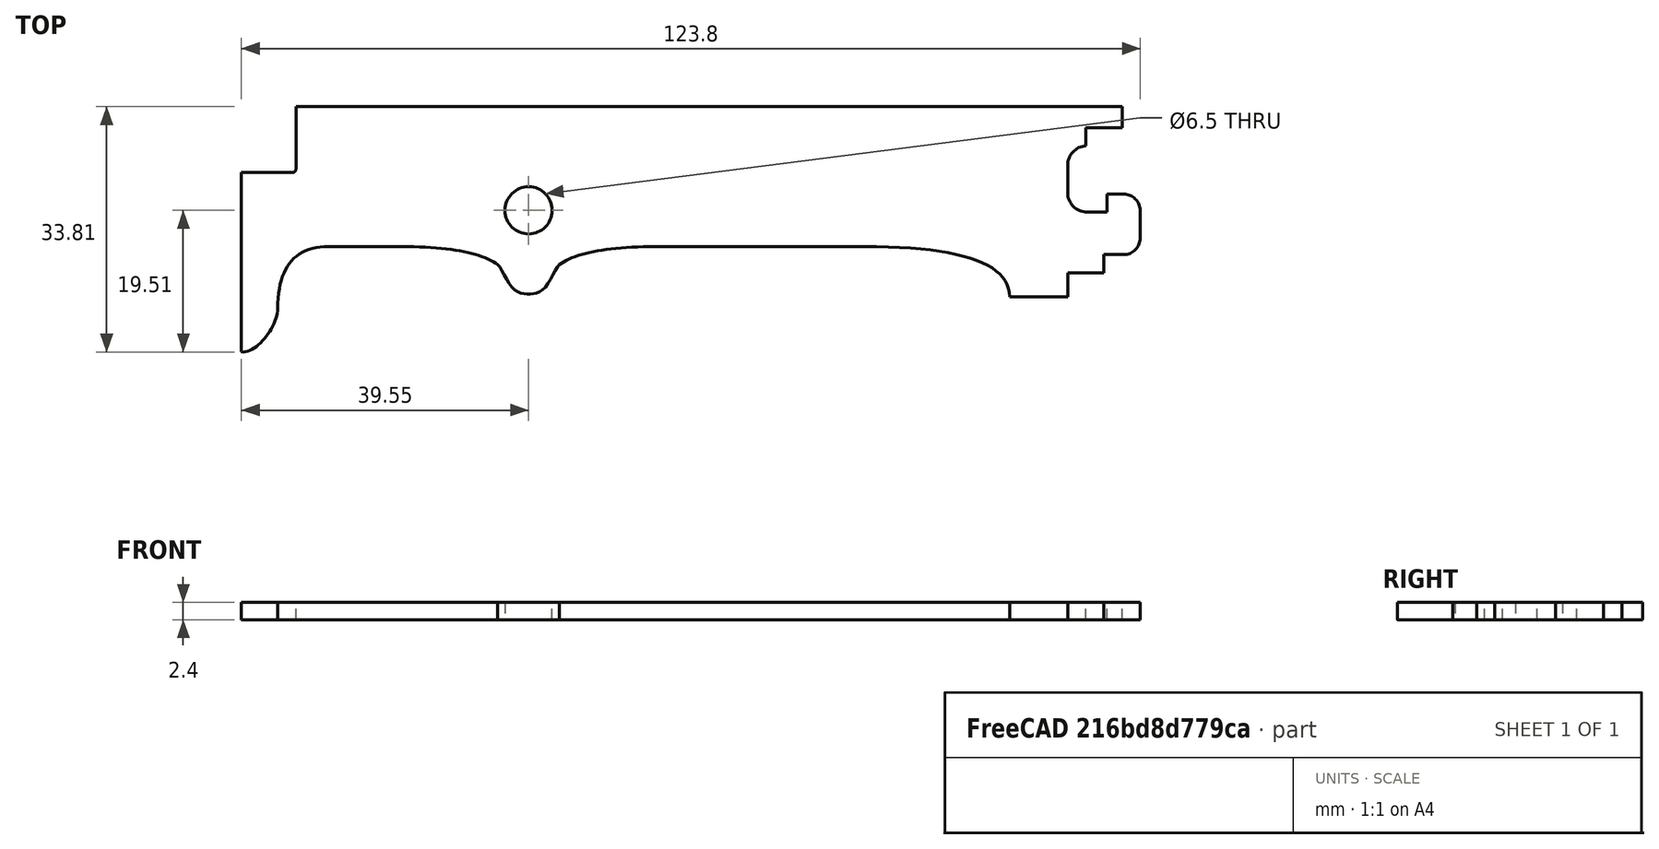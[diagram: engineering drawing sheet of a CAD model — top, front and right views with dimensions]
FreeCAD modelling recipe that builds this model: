
FCSTD DOCUMENT  (FreeCAD 0.19R0.19.2)
Label: v0_14
License: All rights reserved
LicenseURL: http://en.wikipedia.org/wiki/All_rights_reserved
objects: Sketcher::SketchObject×2, Part::Extrusion×1
note: 3 computed .brp shape members not serialized (recipe doc carries the construction recipe); baked Part::Feature solids carry a one-line shape summary decoded from their .brp

FEATURE [Sketcher::SketchObject] Sketch
  FullyConstrained = true
  sketch-geometry (69):
    g0: ArcOfCircle CenterX=-20 CenterY=-14.35 CenterZ=0 NormalX=0 NormalY=0 NormalZ=1 AngleXU=0 Radius=2.3 StartAngle=8e-16 EndAngle=1.5708
    g1: ArcOfCircle CenterX=-20 CenterY=-18.1 CenterZ=0 NormalX=0 NormalY=0 NormalZ=1 AngleXU=0 Radius=2.3 StartAngle=4.71239 EndAngle=6.28319
    g2: LineSegment StartX=-20 StartY=-20.4 StartZ=0 EndX=-22.7 EndY=-20.4 EndZ=0
    g3: LineSegment StartX=-22.7 StartY=-22.9 StartZ=0 EndX=-22.7 EndY=-20.4 EndZ=0
    g4: LineSegment StartX=-17.7 StartY=-14.35 StartZ=0 EndX=-17.7 EndY=-18.1 EndZ=0
    g5: LineSegment StartX=-25.2 StartY=-5.40742 StartZ=0 EndX=-25.2 EndY=-2.9 EndZ=0
    g6: LineSegment StartX=-25.2 StartY=-2.9 StartZ=0 EndX=-20.2 EndY=-2.9 EndZ=0
    g7: LineSegment StartX=-20.2 StartY=-2.9 StartZ=0 EndX=-20.2 EndY=0 EndZ=0
    g8: ArcOfCircle CenterX=-25 CenterY=-8.1 CenterZ=0 NormalX=0 NormalY=0 NormalZ=1 AngleXU=0 Radius=2.7 StartAngle=1.64494 EndAngle=3.14159
    g9: ArcOfCircle CenterX=-25 CenterY=-11.85 CenterZ=0 NormalX=0 NormalY=0 NormalZ=1 AngleXU=0 Radius=2.7 StartAngle=3.14159 EndAngle=4.71239
    g10: LineSegment StartX=-27.7 StartY=-8.1 StartZ=0 EndX=-27.7 EndY=-11.85 EndZ=0
    g11: LineSegment StartX=-25 StartY=-14.55 StartZ=0 EndX=-22.3 EndY=-14.55 EndZ=0
    g12: LineSegment StartX=-22.3 StartY=-12.05 StartZ=0 EndX=-22.3 EndY=-14.55 EndZ=0
    g13: LineSegment StartX=-22.3 StartY=-12.05 StartZ=0 EndX=-20 EndY=-12.05 EndZ=0
    g14: LineSegment StartX=-27.7 StartY=-22.9 StartZ=0 EndX=-22.7 EndY=-22.9 EndZ=0
    g15: LineSegment StartX=-27.7 StartY=-22.9 StartZ=0 EndX=-27.7 EndY=-26.2 EndZ=0
    g16: Circle CenterX=-101.95 CenterY=-14.3 CenterZ=0 NormalX=0 NormalY=0 NormalZ=1 AngleXU=0 Radius=3.25
    g17: LineSegment StartX=-134 StartY=0 StartZ=0 EndX=-20.2 EndY=0 EndZ=0
    g18: LineSegment StartX=-134 StartY=2.68e-14 StartZ=0 EndX=-134 EndY=-8.6 EndZ=0
    g19: LineSegment StartX=-134.5 StartY=-9.1 StartZ=0 EndX=-141.5 EndY=-9.1 EndZ=0
    g20: ArcOfCircle CenterX=-134.5 CenterY=-8.6 CenterZ=0 NormalX=0 NormalY=0 NormalZ=1 AngleXU=0 Radius=0.5 StartAngle=4.71239 EndAngle=6.28319
    g21: Circle CenterX=-97.7 CenterY=-21.8 CenterZ=0 NormalX=0 NormalY=0 NormalZ=1 AngleXU=0 Radius=1
    g22: Circle CenterX=-94.45 CenterY=-19.3 CenterZ=0 NormalX=0 NormalY=0 NormalZ=1 AngleXU=0 Radius=1
    g23: Circle CenterX=-84.45 CenterY=-19.3 CenterZ=0 NormalX=0 NormalY=0 NormalZ=1 AngleXU=0 Radius=1
    g24: BSplineCurve PolesCount=3 KnotsCount=2 Degree=2 IsPeriodic=0
    g25: GeomPoint X=-97.7 Y=-21.8 Z=0
    g26: GeomPoint X=-84.45 Y=-19.3 Z=0
    g27: Circle CenterX=-106.2 CenterY=-21.8 CenterZ=0 NormalX=0 NormalY=0 NormalZ=1 AngleXU=0 Radius=1
    g28: Circle CenterX=-109.45 CenterY=-19.3 CenterZ=0 NormalX=0 NormalY=0 NormalZ=1 AngleXU=0 Radius=1
    g29: Circle CenterX=-119.45 CenterY=-19.3 CenterZ=0 NormalX=0 NormalY=0 NormalZ=1 AngleXU=0 Radius=1
    g30: BSplineCurve PolesCount=3 KnotsCount=2 Degree=2 IsPeriodic=0
    g31: GeomPoint X=-106.2 Y=-21.8 Z=0
    g32: GeomPoint X=-119.45 Y=-19.3 Z=0
    g33: LineSegment StartX=-141.5 StartY=-9.1 StartZ=0 EndX=-141.5 EndY=-33.8 EndZ=0
    g34-g37: Circle x4 (B-spline internal-alignment scaffolding for g38; pole/knot coordinates omitted)
    g38: BSplineCurve PolesCount=4 KnotsCount=2 Degree=3 IsPeriodic=0
    g39: GeomPoint X=-141.5 Y=-33.8 Z=0
    g40: GeomPoint X=-136.5 Y=-27.8 Z=0
    g41: Circle CenterX=-136.5 CenterY=-27.8 CenterZ=0 NormalX=0 NormalY=0 NormalZ=1 AngleXU=0 Radius=1
    g42: Circle CenterX=-136.5 CenterY=-19.3 CenterZ=0 NormalX=0 NormalY=0 NormalZ=1 AngleXU=0 Radius=1
    g43: Circle CenterX=-129.5 CenterY=-19.3 CenterZ=0 NormalX=0 NormalY=0 NormalZ=1 AngleXU=0 Radius=1
    g44: BSplineCurve PolesCount=3 KnotsCount=2 Degree=2 IsPeriodic=0
    g45: GeomPoint X=-136.5 Y=-27.8 Z=0
    g46: GeomPoint X=-129.5 Y=-19.3 Z=0
    g47: LineSegment StartX=-129.5 StartY=-19.3 StartZ=0 EndX=-119.45 EndY=-19.3 EndZ=0
    g48: LineSegment StartX=-35.7 StartY=-26.2 StartZ=0 EndX=-27.7 EndY=-26.2 EndZ=0
    g49: Circle CenterX=-35.7 CenterY=-26.2 CenterZ=0 NormalX=0 NormalY=0 NormalZ=1 AngleXU=0 Radius=1
    g50: Circle CenterX=-35.7 CenterY=-19.3 CenterZ=0 NormalX=0 NormalY=0 NormalZ=1 AngleXU=0 Radius=1
    g51: Circle CenterX=-55.7 CenterY=-19.3 CenterZ=0 NormalX=0 NormalY=0 NormalZ=1 AngleXU=0 Radius=1
    g52: BSplineCurve PolesCount=3 KnotsCount=2 Degree=2 IsPeriodic=0
    g53: GeomPoint X=-35.7 Y=-26.2 Z=0
    g54: GeomPoint X=-55.7 Y=-19.3 Z=0
    g55: LineSegment StartX=-84.45 StartY=-19.3 StartZ=0 EndX=-55.7 EndY=-19.3 EndZ=0
    g56-g62: Circle x7 (B-spline internal-alignment scaffolding for g63; pole/knot coordinates omitted)
    g63: BSplineCurve PolesCount=7 KnotsCount=5 Degree=3 IsPeriodic=0
    g64-g68: GeomPoint x5 (B-spline internal-alignment scaffolding for g63; pole/knot coordinates omitted)
  constraints (111):
    c: Block(g1)
    c: Block(g0)
    c: Coincident(g2,g1)
    c: Horizontal(g2)
    c: Vertical(g3)
    c: Coincident(g3,g2)
    c: Coincident(g4,g0)
    c: Coincident(g4,g1)
    c: Vertical(g4)
    c: Vertical(g5)
    c: Block(g5)
    c: Coincident(g6,g5)
    c: Horizontal(g6)
    c: Vertical(g7)
    c: Block(g7)
    c: Block(g6)
    c: Coincident(g8,g5)
    c: Block(g9)
    c: Coincident(g10,g8)
    c: Coincident(g10,g9)
    c: Vertical(g10)
    c: Block(g10)
    c: Coincident(g11,g9)
    c: Horizontal(g11)
    c: Vertical(g12)
    c: Coincident(g12,g11)
    c: Block(g12)
    c: Coincident(g13,g0)
    c: Horizontal(g13)
    c: Block(g13)
    c: Coincident(g14,g3)
    c: Horizontal(g14)
    c: Block(g14)
    c: Coincident(g15,g14)
    c: Vertical(g15)
    c: Block(g16)
    c: Coincident(g17,g7)
    c: Horizontal(g17)
    c: Vertical(g18)
    c: Distance(g18) = 8.6
    c: Horizontal(g19)
    c: Distance(g19) = 7
    c: Coincident(g20,g18)
    c: Coincident(g20,g19)
    c: Block(g20)
    c: Block(g17)
    c: Weight(g21) = 1
    c: Equal(g21,g22)
    c: Equal(g21,g23)
    c: InternalAlignment(g21,g24)
    c: InternalAlignment(g22,g24)
    c: InternalAlignment(g23,g24)
    c: InternalAlignment(g25,g24)
    c: InternalAlignment(g26,g24)
    c: Weight(g27) = 1
    c: Equal(g27,g28)
    c: Equal(g27,g29)
    c: InternalAlignment(g27,g30)
    c: InternalAlignment(g28,g30)
    c: InternalAlignment(g29,g30)
    c: InternalAlignment(g31,g30)
    c: InternalAlignment(g32,g30)
    c: Block(g30)
    c: Block(g24)
    c: Coincident(g33,g19)
    c: Vertical(g33)
    c: Block(g33)
    c: Coincident(g38,g33)
    c: Weight(g34) = 1
    c: Equal(g34,g35)
    c: Equal(g34,g36)
    c: Equal(g34,g37)
    c: InternalAlignment(g34-g37 -> g38) x4
    c: InternalAlignment(g39,g38)
    c: InternalAlignment(g40,g38)
    c: Weight(g41) = 1
    c: Equal(g41,g42)
    c: Equal(g41,g43)
    c: InternalAlignment(g41,g44)
    c: InternalAlignment(g42,g44)
    c: InternalAlignment(g43,g44)
    c: InternalAlignment(g45,g44)
    c: InternalAlignment(g46,g44)
    c: Block(g38)
    c: Block(g44)
    c: Coincident(g47,g44)
    c: Coincident(g47,g30)
    c: Horizontal(g47)
    c: Horizontal(g48)
    c: Distance(g48) = 8
    c: Block(g48)
    c: Block(g15)
    c: Block(g8)
    c: Coincident(g52,g48)
    c: Weight(g49) = 1
    c: Equal(g49,g50)
    c: Equal(g49,g51)
    c: InternalAlignment(g49,g52)
    c: InternalAlignment(g50,g52)
    c: InternalAlignment(g51,g52)
    c: InternalAlignment(g53,g52)
    c: InternalAlignment(g54,g52)
    c: Block(g52)
    c: Coincident(g55,g24)
    c: Coincident(g55,g52)
    c: Horizontal(g55)
    c: Weight(g56) = 1
    c: Equal(g56, g57-g62) x6
    c: InternalAlignment(g56-g62 -> g63) x7
    c: InternalAlignment(g64-g68 -> g63) x5
    c: Block(g63)
FEATURE [Part::Extrusion] Extrude
  Base = -> Sketch
  Dir = (0,0,1)
  DirMode = 2
  FaceMakerClass = Part::FaceMakerBullseye
  LengthFwd = 2.4
  LengthRev = 0
  Solid = true
  Symmetric = false
FEATURE [Sketcher::SketchObject] Sketch001
  FullyConstrained = true
  sketch-geometry (99):
    g0: ArcOfCircle CenterX=-20 CenterY=-14.35 CenterZ=0 NormalX=0 NormalY=0 NormalZ=1 AngleXU=0 Radius=2.3 StartAngle=8e-16 EndAngle=1.5708
    g1: ArcOfCircle CenterX=-20 CenterY=-18.1 CenterZ=0 NormalX=0 NormalY=0 NormalZ=1 AngleXU=0 Radius=2.3 StartAngle=4.71239 EndAngle=6.28319
    g2: LineSegment StartX=-20 StartY=-20.4 StartZ=0 EndX=-22.7 EndY=-20.4 EndZ=0
    g3: LineSegment StartX=-22.7 StartY=-22.9 StartZ=0 EndX=-22.7 EndY=-20.4 EndZ=0
    g4: LineSegment StartX=-17.7 StartY=-14.35 StartZ=0 EndX=-17.7 EndY=-18.1 EndZ=0
    g5: LineSegment StartX=-25.2 StartY=-5.40742 StartZ=0 EndX=-25.2 EndY=-2.9 EndZ=0
    g6: LineSegment StartX=-25.2 StartY=-2.9 StartZ=0 EndX=-20.2 EndY=-2.9 EndZ=0
    g7: LineSegment StartX=-20.2 StartY=-2.9 StartZ=0 EndX=-20.2 EndY=0 EndZ=0
    g8: ArcOfCircle CenterX=-25 CenterY=-8.1 CenterZ=0 NormalX=0 NormalY=0 NormalZ=1 AngleXU=0 Radius=2.7 StartAngle=1.64494 EndAngle=3.14159
    g9: ArcOfCircle CenterX=-25 CenterY=-11.85 CenterZ=0 NormalX=0 NormalY=0 NormalZ=1 AngleXU=0 Radius=2.7 StartAngle=3.14159 EndAngle=4.71239
    g10: LineSegment StartX=-27.7 StartY=-8.1 StartZ=0 EndX=-27.7 EndY=-11.85 EndZ=0
    g11: LineSegment StartX=-25 StartY=-14.55 StartZ=0 EndX=-22.3 EndY=-14.55 EndZ=0
    g12: LineSegment StartX=-22.3 StartY=-12.05 StartZ=0 EndX=-22.3 EndY=-14.55 EndZ=0
    g13: LineSegment StartX=-22.3 StartY=-12.05 StartZ=0 EndX=-20 EndY=-12.05 EndZ=0
    g14: LineSegment StartX=-27.7 StartY=-22.9 StartZ=0 EndX=-22.7 EndY=-22.9 EndZ=0
    g15: LineSegment StartX=-27.7 StartY=-22.9 StartZ=0 EndX=-27.7 EndY=-26.2 EndZ=0
    g16: Circle CenterX=-101.95 CenterY=-14.3 CenterZ=0 NormalX=0 NormalY=0 NormalZ=1 AngleXU=0 Radius=3.25
    g17: LineSegment StartX=-134 StartY=0 StartZ=0 EndX=-134 EndY=-8.6 EndZ=0
    g18: LineSegment StartX=-134.5 StartY=-9.1 StartZ=0 EndX=-141.5 EndY=-9.1 EndZ=0
    g19: ArcOfCircle CenterX=-134.5 CenterY=-8.6 CenterZ=0 NormalX=0 NormalY=0 NormalZ=1 AngleXU=0 Radius=0.5 StartAngle=4.71239 EndAngle=6.28319
    g20: Circle CenterX=-97.7 CenterY=-21.8 CenterZ=0 NormalX=0 NormalY=0 NormalZ=1 AngleXU=0 Radius=1
    g21: Circle CenterX=-94.45 CenterY=-19.3 CenterZ=0 NormalX=0 NormalY=0 NormalZ=1 AngleXU=0 Radius=1
    g22: Circle CenterX=-84.45 CenterY=-19.3 CenterZ=0 NormalX=0 NormalY=0 NormalZ=1 AngleXU=0 Radius=1
    g23: BSplineCurve PolesCount=3 KnotsCount=2 Degree=2 IsPeriodic=0
    g24: GeomPoint X=-97.7 Y=-21.8 Z=0
    g25: GeomPoint X=-84.45 Y=-19.3 Z=0
    g26: Circle CenterX=-106.2 CenterY=-21.8 CenterZ=0 NormalX=0 NormalY=0 NormalZ=1 AngleXU=0 Radius=1
    g27: Circle CenterX=-109.45 CenterY=-19.3 CenterZ=0 NormalX=0 NormalY=0 NormalZ=1 AngleXU=0 Radius=1
    g28: Circle CenterX=-119.45 CenterY=-19.3 CenterZ=0 NormalX=0 NormalY=0 NormalZ=1 AngleXU=0 Radius=1
    g29: BSplineCurve PolesCount=3 KnotsCount=2 Degree=2 IsPeriodic=0
    g30: GeomPoint X=-106.2 Y=-21.8 Z=0
    g31: GeomPoint X=-119.45 Y=-19.3 Z=0
    g32: LineSegment StartX=-141.5 StartY=-9.1 StartZ=0 EndX=-141.5 EndY=-33.8 EndZ=0
    g33-g36: Circle x4 (B-spline internal-alignment scaffolding for g37; pole/knot coordinates omitted)
    g37: BSplineCurve PolesCount=4 KnotsCount=2 Degree=3 IsPeriodic=0
    g38: GeomPoint X=-141.5 Y=-33.8 Z=0
    g39: GeomPoint X=-136.5 Y=-27.8 Z=0
    g40: Circle CenterX=-136.5 CenterY=-27.8 CenterZ=0 NormalX=0 NormalY=0 NormalZ=1 AngleXU=0 Radius=1
    g41: Circle CenterX=-136.5 CenterY=-19.3 CenterZ=0 NormalX=0 NormalY=0 NormalZ=1 AngleXU=0 Radius=1
    g42: Circle CenterX=-129.5 CenterY=-19.3 CenterZ=0 NormalX=0 NormalY=0 NormalZ=1 AngleXU=0 Radius=1
    g43: BSplineCurve PolesCount=3 KnotsCount=2 Degree=2 IsPeriodic=0
    g44: GeomPoint X=-136.5 Y=-27.8 Z=0
    g45: GeomPoint X=-129.5 Y=-19.3 Z=0
    g46: LineSegment StartX=-129.5 StartY=-19.3 StartZ=0 EndX=-119.45 EndY=-19.3 EndZ=0
    g47: LineSegment StartX=-35.7 StartY=-26.2 StartZ=0 EndX=-27.7 EndY=-26.2 EndZ=0
    g48: Circle CenterX=-35.7 CenterY=-26.2 CenterZ=0 NormalX=0 NormalY=0 NormalZ=1 AngleXU=0 Radius=1
    g49: Circle CenterX=-35.7 CenterY=-19.3 CenterZ=0 NormalX=0 NormalY=0 NormalZ=1 AngleXU=0 Radius=1
    g50: Circle CenterX=-55.7 CenterY=-19.3 CenterZ=0 NormalX=0 NormalY=0 NormalZ=1 AngleXU=0 Radius=1
    g51: BSplineCurve PolesCount=3 KnotsCount=2 Degree=2 IsPeriodic=0
    g52: GeomPoint X=-35.7 Y=-26.2 Z=0
    g53: GeomPoint X=-55.7 Y=-19.3 Z=0
    g54: LineSegment StartX=-84.45 StartY=-19.3 StartZ=0 EndX=-55.7 EndY=-19.3 EndZ=0
    g55-g61: Circle x7 (B-spline internal-alignment scaffolding for g62; pole/knot coordinates omitted)
    g62: BSplineCurve PolesCount=7 KnotsCount=5 Degree=3 IsPeriodic=0
    g63-g67: GeomPoint x5 (B-spline internal-alignment scaffolding for g62; pole/knot coordinates omitted)
    g68: LineSegment StartX=-134 StartY=0 StartZ=0 EndX=-20.2 EndY=0 EndZ=0
    g69: ArcOfCircle CenterX=-101.95 CenterY=-14.3 CenterZ=0 NormalX=0 NormalY=0 NormalZ=1 AngleXU=0 Radius=4.69707 StartAngle=3.58144 EndAngle=5.84334
    g70: Circle CenterX=-40.7 CenterY=-3 CenterZ=0 NormalX=0 NormalY=0 NormalZ=1 AngleXU=0 Radius=1
    g71: Circle CenterX=-35.7 CenterY=-3 CenterZ=0 NormalX=0 NormalY=0 NormalZ=1 AngleXU=0 Radius=1
    g72: Circle CenterX=-35.7 CenterY=-8 CenterZ=0 NormalX=0 NormalY=0 NormalZ=1 AngleXU=0 Radius=1
    g73: BSplineCurve PolesCount=3 KnotsCount=2 Degree=2 IsPeriodic=0
    g74: GeomPoint X=-40.7 Y=-3 Z=0
    g75: GeomPoint X=-35.7 Y=-8 Z=0
    g76: Circle CenterX=-35.7 CenterY=-11.3 CenterZ=0 NormalX=0 NormalY=0 NormalZ=1 AngleXU=0 Radius=1
    g77: Circle CenterX=-35.7 CenterY=-16.3 CenterZ=0 NormalX=0 NormalY=0 NormalZ=1 AngleXU=0 Radius=1
    g78: Circle CenterX=-40.7 CenterY=-16.3 CenterZ=0 NormalX=0 NormalY=0 NormalZ=1 AngleXU=0 Radius=1
    g79: BSplineCurve PolesCount=3 KnotsCount=2 Degree=2 IsPeriodic=0
    g80: GeomPoint X=-35.7 Y=-11.3 Z=0
    g81: GeomPoint X=-40.7 Y=-16.3 Z=0
    g82: Circle CenterX=-124.5 CenterY=-16.3 CenterZ=0 NormalX=0 NormalY=0 NormalZ=1 AngleXU=0 Radius=1
    g83: Circle CenterX=-129.5 CenterY=-16.3 CenterZ=0 NormalX=0 NormalY=0 NormalZ=1 AngleXU=0 Radius=1
    g84: Circle CenterX=-129.5 CenterY=-11.3 CenterZ=0 NormalX=0 NormalY=0 NormalZ=1 AngleXU=0 Radius=1
    g85: BSplineCurve PolesCount=3 KnotsCount=2 Degree=2 IsPeriodic=0
    g86: GeomPoint X=-124.5 Y=-16.3 Z=0
    g87: GeomPoint X=-129.5 Y=-11.3 Z=0
    g88: Circle CenterX=-129.5 CenterY=-8 CenterZ=0 NormalX=0 NormalY=0 NormalZ=1 AngleXU=0 Radius=1
    g89: Circle CenterX=-129.5 CenterY=-3 CenterZ=0 NormalX=0 NormalY=0 NormalZ=1 AngleXU=0 Radius=1
    g90: Circle CenterX=-124.5 CenterY=-3 CenterZ=0 NormalX=0 NormalY=0 NormalZ=1 AngleXU=0 Radius=1
    g91: BSplineCurve PolesCount=3 KnotsCount=2 Degree=2 IsPeriodic=0
    g92: GeomPoint X=-129.5 Y=-8 Z=0
    g93: GeomPoint X=-124.5 Y=-3 Z=0
    g94: LineSegment StartX=-129.5 StartY=-8 StartZ=0 EndX=-129.5 EndY=-11.3 EndZ=0
    g95: LineSegment StartX=-124.5 StartY=-3 StartZ=0 EndX=-40.7 EndY=-3 EndZ=0
    g96: LineSegment StartX=-35.7 StartY=-8 StartZ=0 EndX=-35.7 EndY=-11.3 EndZ=0
    g97: LineSegment StartX=-40.7 StartY=-16.3 StartZ=0 EndX=-97.7 EndY=-16.3 EndZ=0
    g98: LineSegment StartX=-106.2 StartY=-16.3 StartZ=0 EndX=-124.5 EndY=-16.3 EndZ=0
  constraints (164):
    c: Block(g1)
    c: Block(g0)
    c: Coincident(g2,g1)
    c: Horizontal(g2)
    c: Vertical(g3)
    c: Coincident(g3,g2)
    c: Coincident(g4,g0)
    c: Coincident(g4,g1)
    c: Vertical(g4)
    c: Vertical(g5)
    c: Block(g5)
    c: Coincident(g6,g5)
    c: Horizontal(g6)
    c: Vertical(g7)
    c: Block(g7)
    c: Block(g6)
    c: Coincident(g8,g5)
    c: Block(g9)
    c: Coincident(g10,g8)
    c: Coincident(g10,g9)
    c: Vertical(g10)
    c: Block(g10)
    c: Coincident(g11,g9)
    c: Horizontal(g11)
    c: Vertical(g12)
    c: Coincident(g12,g11)
    c: Block(g12)
    c: Coincident(g13,g0)
    c: Horizontal(g13)
    c: Block(g13)
    c: Coincident(g14,g3)
    c: Horizontal(g14)
    c: Block(g14)
    c: Coincident(g15,g14)
    c: Vertical(g15)
    c: Block(g16)
    c: Vertical(g17)
    c: Distance(g17) = 8.6
    c: Horizontal(g18)
    c: Distance(g18) = 7
    c: Coincident(g19,g17)
    c: Coincident(g19,g18)
    c: Block(g19)
    c: Weight(g20) = 1
    c: Equal(g20,g21)
    c: Equal(g20,g22)
    c: InternalAlignment(g20,g23)
    c: InternalAlignment(g21,g23)
    c: InternalAlignment(g22,g23)
    c: InternalAlignment(g24,g23)
    c: InternalAlignment(g25,g23)
    c: Weight(g26) = 1
    c: Equal(g26,g27)
    c: Equal(g26,g28)
    c: InternalAlignment(g26,g29)
    c: InternalAlignment(g27,g29)
    c: InternalAlignment(g28,g29)
    c: InternalAlignment(g30,g29)
    c: InternalAlignment(g31,g29)
    c: Block(g23)
    c: Coincident(g32,g18)
    c: Vertical(g32)
    c: Block(g32)
    c: Coincident(g37,g32)
    c: Weight(g33) = 1
    c: Equal(g33,g34)
    c: Equal(g33,g35)
    c: Equal(g33,g36)
    c: InternalAlignment(g33-g36 -> g37) x4
    c: InternalAlignment(g38,g37)
    c: InternalAlignment(g39,g37)
    c: Weight(g40) = 1
    c: Equal(g40,g41)
    c: Equal(g40,g42)
    c: InternalAlignment(g40,g43)
    c: InternalAlignment(g41,g43)
    c: InternalAlignment(g42,g43)
    c: InternalAlignment(g44,g43)
    c: InternalAlignment(g45,g43)
    c: Block(g37)
    c: Coincident(g46,g43)
    c: Coincident(g46,g29)
    c: Horizontal(g46)
    c: Horizontal(g47)
    c: Distance(g47) = 8
    c: Block(g47)
    c: Block(g15)
    c: Block(g8)
    c: Coincident(g51,g47)
    c: Weight(g48) = 1
    c: Equal(g48,g49)
    c: Equal(g48,g50)
    c: InternalAlignment(g48,g51)
    c: InternalAlignment(g49,g51)
    c: InternalAlignment(g50,g51)
    c: InternalAlignment(g52,g51)
    c: InternalAlignment(g53,g51)
    c: Block(g51)
    c: Coincident(g54,g23)
    c: Coincident(g54,g51)
    c: Horizontal(g54)
    c: Weight(g55) = 1
    c: Equal(g55, g56-g61) x6
    c: InternalAlignment(g55-g61 -> g62) x7
    c: InternalAlignment(g63-g67 -> g62) x5
    c: Block(g62)
    c: Coincident(g68,g17)
    c: Coincident(g68,g7)
    c: Horizontal(g68)
    c: Coincident(g69,g16)
    c: Block(g69)
    c: Block(g29)
    c: Block(g43)
    c: Weight(g70) = 1
    c: Equal(g70,g71)
    c: Equal(g70,g72)
    c: InternalAlignment(g70,g73)
    c: InternalAlignment(g71,g73)
    c: InternalAlignment(g72,g73)
    c: InternalAlignment(g74,g73)
    c: InternalAlignment(g75,g73)
    c: Weight(g76) = 1
    c: Equal(g76,g77)
    c: Equal(g76,g78)
    c: InternalAlignment(g76,g79)
    c: InternalAlignment(g77,g79)
    c: InternalAlignment(g78,g79)
    c: InternalAlignment(g80,g79)
    c: InternalAlignment(g81,g79)
    c: Weight(g82) = 1
    c: Equal(g82,g83)
    c: Equal(g82,g84)
    c: InternalAlignment(g82,g85)
    c: InternalAlignment(g83,g85)
    c: InternalAlignment(g84,g85)
    c: InternalAlignment(g86,g85)
    c: InternalAlignment(g87,g85)
    c: Weight(g88) = 1
    c: Equal(g88,g89)
    c: Equal(g88,g90)
    c: InternalAlignment(g88,g91)
    c: InternalAlignment(g89,g91)
    c: InternalAlignment(g90,g91)
    c: InternalAlignment(g92,g91)
    c: InternalAlignment(g93,g91)
    c: Block(g91)
    c: Block(g85)
    c: Block(g79)
    c: Block(g73)
    c: Coincident(g94,g91)
    c: Coincident(g94,g85)
    c: Vertical(g94)
    c: Coincident(g95,g91)
    c: Horizontal(g95)
    c: Coincident(g96,g73)
    c: Coincident(g96,g79)
    c: Vertical(g96)
    c: Coincident(g97,g79)
    c: Coincident(g97,g69)
    c: Horizontal(g97)
    c: Coincident(g98,g69)
    c: Coincident(g98,g85)
    c: Horizontal(g98)
    c: Block(g95)
